# Revit family: NLRS_33_GM_FB_TC_STORAX_vloerluik_BVS-400_BCB
name_source: partatom
category: Generic Models
revit_build: Autodesk Revit 2014 (Build: 20130308_1515(x64)
units: mm (PartAtom-declared; Revit-internal decimal feet)

## types (4) — shared parameters
Manufacturer = Storax
Model = BV
URL = http://www.storax.nl
belasting = 400 kN
binnenluik = tbv betonvulling
brandwerend 90 min = nee
gasdrukveer = nee
geïsoleerd = ja
materiaal = bcb_staal
productgroep = Vloerluiken
rubberen_afdichting = enkel
scharnierend = nee
sluiting = 4
vergrendeling = nee
vullen_met_beton = ja

## per-type parameters (varying)
| type | Default Elevation | binnenmaat_breedte | binnenmaat_lengte | gewicht | liggers_lengte | uitwendige_breedte | uitwendige_lengte | versterking_110 | versterking_66 | versterking_88 |
| BVS-400 66 | 1219 mm | 600 mm | 600 mm | 62 | 647 mm  [stored 2.1227 ft] | 815 mm  [stored 2.67388 ft] | 735 mm | No | Yes | No |
| BVS-400 88 | 1219 mm | 800 mm  [stored 2.62467 ft] | 800 mm  [stored 2.62467 ft] | 103 | 847 mm  [stored 2.77887 ft] | 1015 mm  [stored 3.33005 ft] | 935 mm | No | No | Yes |
| BVS-400 110 | 0 mm  [stored 0 ft] | 1000 mm  [stored 3.28084 ft] | 1000 mm  [stored 3.28084 ft] | 175 | 1047 mm  [stored 3.43504 ft] | 1215 mm  [stored 3.98622 ft] | 1135 mm  [stored 3.72375 ft] | Yes | No | No |
| maatwerk | 0 mm  [stored 0 ft] | 1000 mm  [stored 3.28084 ft] | 1000 mm  [stored 3.28084 ft] | 0 | 1047 mm  [stored 3.43504 ft] | 1215 mm  [stored 3.98622 ft] | 1135 mm  [stored 3.72375 ft] | Yes | No | No |

note: [stored X ft] marks values corroborated as IEEE doubles in the binary element streams (Revit-internal decimal feet)

## geometry (parser evidence)
native form markers: Blend x764, Sweep x13
no freeform markers — native parametric forms only
